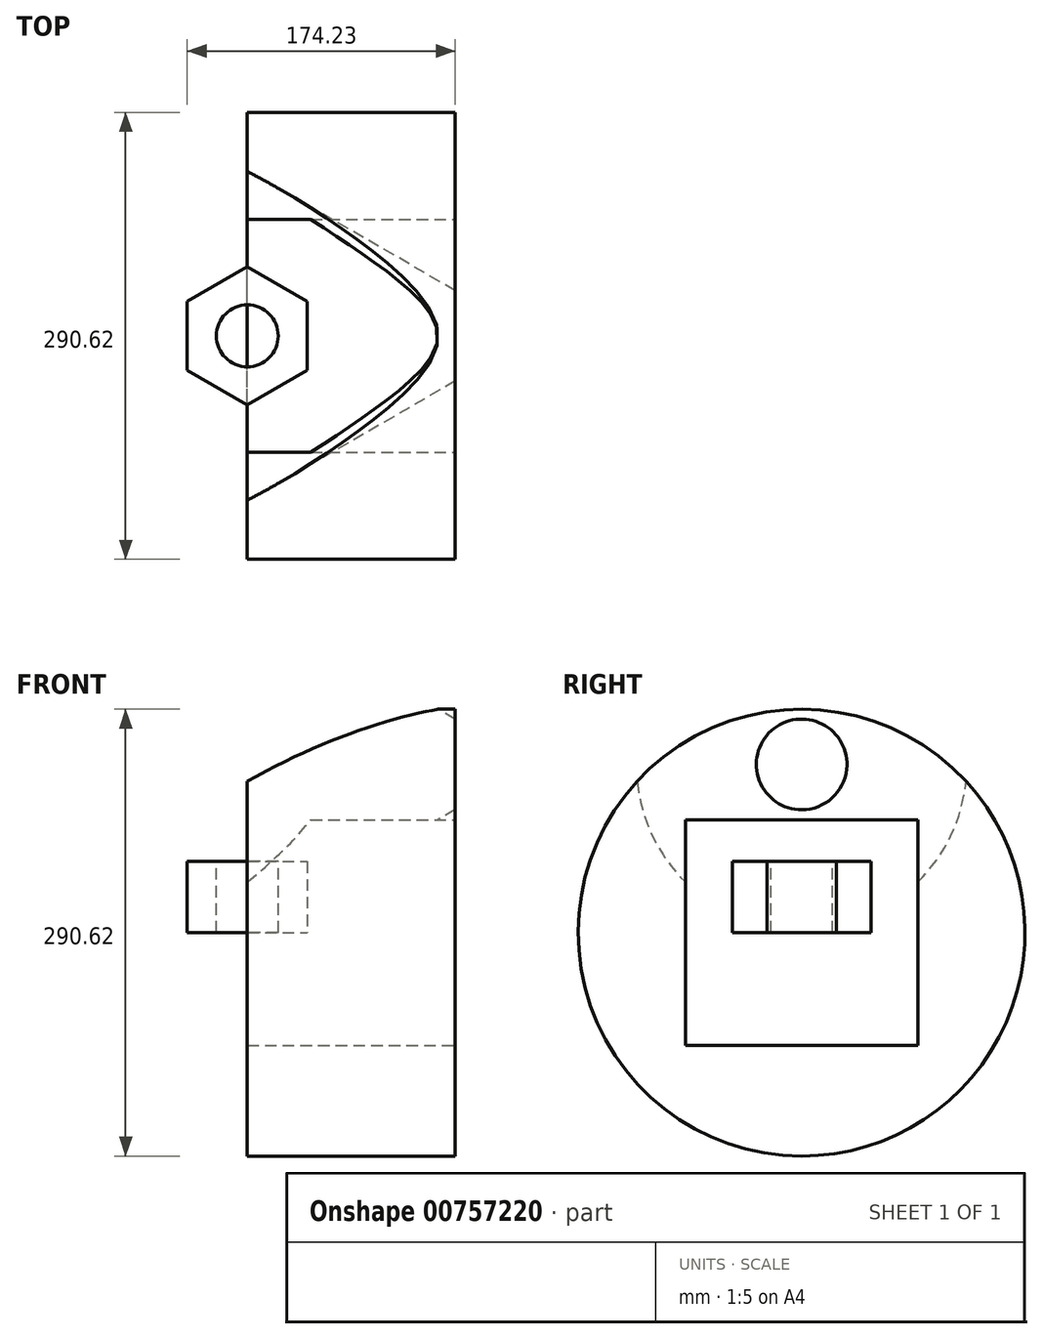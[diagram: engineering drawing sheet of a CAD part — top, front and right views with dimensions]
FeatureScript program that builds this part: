
annotation { "Feature Type Name" : "Feature", "Feature Type Description" : "" }
export const myFeature = defineFeature(function(context is Context, id is Id, definition is map)
    precondition{}
    {
        {
            var Q0;
            Q0=qCreatedBy(makeId("Top.planeOp"),FACE);
            var sketch = newSketch(context, id + "F0", { "sketchPlane" : qUnion([Q0])});
            skCircle(sketch, "E0.cCircle", {"center": v(0, 0) * mm, "radius": 44.06 * mm, "construction": true});
            skLineSegment(sketch, "E0.0", {"start": v(26.59, 38.63) * mm, "end": v(45.2, 12.5) * mm});
            skLineSegment(sketch, "E0.1", {"start": v(45.2, 12.5) * mm, "end": v(42.66, -19.48) * mm});
            skLineSegment(sketch, "E0.2", {"start": v(42.66, -19.48) * mm, "end": v(20.16, -42.34) * mm});
            skLineSegment(sketch, "E0.3", {"start": v(20.16, -42.34) * mm, "end": v(-11.77, -45.4) * mm});
            skLineSegment(sketch, "E0.4", {"start": v(-11.77, -45.4) * mm, "end": v(-38.2, -27.2) * mm});
            skLineSegment(sketch, "E0.5", {"start": v(-38.2, -27.2) * mm, "end": v(-46.75, 3.71) * mm});
            skLineSegment(sketch, "E0.6", {"start": v(-46.75, 3.71) * mm, "end": v(-33.42, 32.9) * mm});
            skLineSegment(sketch, "E0.7", {"start": v(-33.42, 32.9) * mm, "end": v(-4.46, 46.68) * mm});
            skLineSegment(sketch, "E0.8", {"start": v(-4.46, 46.68) * mm, "end": v(26.59, 38.63) * mm});
            skPoint(sketch, "E0.0.midPoint", {"position": v(35.9, 25.56) * mm});
            skSolve(sketch);
        }
        {
            var Q0;
            Q0=makeQuery(id+"F0.imprint","IMPRINT",FACE,{"disambiguationData":[TD([[makeQuery(id+"F0.imprint","IMPRINT",EDGE,{"derivedFrom":sQuery(id+"F0.wireOp",EDGE,"E0.0")}),-1.0]])]});
            extrude(context, id + "F1", {"entities" : qUnion([Q0]), "depth" : 67.3 * mm, "offsetDistance" : 25.4 * mm});
        }
        {
            var Q0;
            Q0=makeQuery(id+"F1.opExtrude","CAP_FACE",FACE,{"disambiguationData":[OSD([sQuery(id+"F0.wireOp",EDGE,"E0.0"),sQuery(id+"F0.wireOp",EDGE,"E0.1"),sQuery(id+"F0.wireOp",EDGE,"E0.2"),sQuery(id+"F0.wireOp",EDGE,"E0.3"),sQuery(id+"F0.wireOp",EDGE,"E0.4"),sQuery(id+"F0.wireOp",EDGE,"E0.5"),sQuery(id+"F0.wireOp",EDGE,"E0.6"),sQuery(id+"F0.wireOp",EDGE,"E0.7"),sQuery(id+"F0.wireOp",EDGE,"E0.8")])],"isStart":false});
            var sketch = newSketch(context, id + "F2", { "sketchPlane" : qUnion([Q0])});
            skCircle(sketch, "E1.cCircle", {"center": v(0, 0) * mm, "radius": 13.36 * mm, "construction": true});
            skLineSegment(sketch, "E1.0", {"start": v(13.36, 6.43) * mm, "end": v(13.36, -6.43) * mm});
            skLineSegment(sketch, "E1.1", {"start": v(13.36, -6.43) * mm, "end": v(3.3, -14.46) * mm});
            skLineSegment(sketch, "E1.2", {"start": v(3.3, -14.46) * mm, "end": v(-9.25, -11.6) * mm});
            skLineSegment(sketch, "E1.3", {"start": v(-9.25, -11.6) * mm, "end": v(-14.83, 0) * mm});
            skLineSegment(sketch, "E1.4", {"start": v(-14.83, 0) * mm, "end": v(-9.25, 11.6) * mm});
            skLineSegment(sketch, "E1.5", {"start": v(-9.25, 11.6) * mm, "end": v(3.3, 14.46) * mm});
            skLineSegment(sketch, "E1.6", {"start": v(3.3, 14.46) * mm, "end": v(13.36, 6.43) * mm});
            skPoint(sketch, "E1.0.midPoint", {"position": v(13.36, 0) * mm});
            skSolve(sketch);
        }
        {
            var Q0;
            Q0=makeQuery(id+"F2.imprint","IMPRINT",FACE,{"disambiguationData":[TD([[makeQuery(id+"F2.imprint","IMPRINT",EDGE,{"derivedFrom":sQuery(id+"F2.wireOp",EDGE,"E1.0")}),-1.0]])]});
            extrude(context, id + "F3", {"entities" : qUnion([Q0]), "operationType" : NewBodyOperationType.REMOVE, "oppositeDirection" : true, "depth" : 91.19 * mm, "offsetDistance" : 25.4 * mm});
        }
        {
            var Q0;
            Q0=qCreatedBy(makeId("Right.planeOp"),FACE);
            var sketch = newSketch(context, id + "F4", { "sketchPlane" : qUnion([Q0])});
            skCircle(sketch, "E2", {"center": v(0, 0) * mm, "radius": 145.31 * mm});
            skSolve(sketch);
        }
        {
            var Q0;
            Q0=makeQuery(id+"F4.imprint","IMPRINT",FACE,{"disambiguationData":[TD([[makeQuery(id+"F4.imprint","IMPRINT",EDGE,{"derivedFrom":sQuery(id+"F4.wireOp",EDGE,"E2")}),1.0]])]});
            extrude(context, id + "F5", {"entities" : qUnion([Q0]), "operationType" : NewBodyOperationType.ADD, "depth" : 135.2 * mm, "offsetDistance" : 25.4 * mm});
        }
        {
            var Q0;
            Q0=makeQuery(id+"F5.opExtrude","CAP_FACE",FACE,{"disambiguationData":[OSD([sQuery(id+"F4.wireOp",EDGE,"E2")])],"isStart":false});
            var sketch = newSketch(context, id + "F6", { "sketchPlane" : qUnion([Q0])});
            skLineSegment(sketch, "E3.bottom", {"start": v(-75.64, 73.41) * mm, "end": v(75.64, 73.41) * mm});
            skLineSegment(sketch, "E3.top", {"start": v(-75.64, -73.41) * mm, "end": v(75.64, -73.41) * mm});
            skLineSegment(sketch, "E3.left", {"start": v(-75.64, 73.41) * mm, "end": v(-75.64, -73.41) * mm});
            skLineSegment(sketch, "E3.right", {"start": v(75.64, 73.41) * mm, "end": v(75.64, -73.41) * mm});
            skPoint(sketch, "E3.middle", {"position": v(0, 0) * mm});
            skSolve(sketch);
        }
        {
            var Q0;
            Q0=makeQuery(id+"F6.imprint","IMPRINT",FACE,{"disambiguationData":[TD([[makeQuery(id+"F6.imprint","IMPRINT",EDGE,{"derivedFrom":sQuery(id+"F6.wireOp",EDGE,"E3.bottom")}),-1.0]])]});
            extrude(context, id + "F7", {"entities" : qUnion([Q0]), "operationType" : NewBodyOperationType.REMOVE, "oppositeDirection" : true, "depth" : 219.4 * mm, "offsetDistance" : 25.4 * mm});
        }
        {
            var Q0;
            Q0=makeQuery(id+"F5.opExtrude","CAP_FACE",FACE,{"disambiguationData":[OSD([sQuery(id+"F4.wireOp",EDGE,"E2")])],"isStart":false});
            var sketch = newSketch(context, id + "F8", { "sketchPlane" : qUnion([Q0])});
            skCircle(sketch, "E4", {"center": v(0, 109.4) * mm, "radius": 29.48 * mm});
            skSolve(sketch);
        }
        {
            var Q0;
            Q0 = qSketchRegion(id + "F8", true);
            var Q1;
            Q1=sQuery(id+"F8.wireOp",EDGE,"E4");
            extrude(context, id + "F9", {"entities" : qUnion([Q0]), "operationType" : NewBodyOperationType.REMOVE, "surfaceEntities" : qUnion([Q1]), "endBound" : BoundingType.THROUGH_ALL, "oppositeDirection" : true, "depth" : 25.4 * mm, "offsetDistance" : 25.4 * mm, "hasDraft" : true, "draftAngle" : 30 * degree});
        }
        {
            var Q0;
            Q0=qCreatedBy(makeId("Top.planeOp"),FACE);
            var sketch = newSketch(context, id + "F10", { "sketchPlane" : qUnion([Q0])});
            skCircle(sketch, "E5.cCircle", {"center": v(0, 0) * mm, "radius": 39.03 * mm, "construction": true});
            skLineSegment(sketch, "E5.0", {"start": v(39.03, 22.53) * mm, "end": v(39.03, -22.53) * mm});
            skLineSegment(sketch, "E5.1", {"start": v(39.03, -22.53) * mm, "end": v(0, -45.07) * mm});
            skLineSegment(sketch, "E5.2", {"start": v(0, -45.07) * mm, "end": v(-39.03, -22.53) * mm});
            skLineSegment(sketch, "E5.3", {"start": v(-39.03, -22.53) * mm, "end": v(-39.03, 22.53) * mm});
            skLineSegment(sketch, "E5.4", {"start": v(-39.03, 22.53) * mm, "end": v(0, 45.07) * mm});
            skLineSegment(sketch, "E5.5", {"start": v(0, 45.07) * mm, "end": v(39.03, 22.53) * mm});
            skPoint(sketch, "E5.0.midPoint", {"position": v(39.03, 0) * mm});
            skSolve(sketch);
        }
        {
            var Q0;
            Q0=makeQuery(id+"F10.imprint","IMPRINT",FACE,{"disambiguationData":[TD([[makeQuery(id+"F10.imprint","IMPRINT",EDGE,{"derivedFrom":sQuery(id+"F10.wireOp",EDGE,"E5.0")}),-1.0]])]});
            extrude(context, id + "F11", {"entities" : qUnion([Q0]), "depth" : 46.23 * mm, "offsetDistance" : 25.4 * mm});
        }
        {
            var Q0;
            Q0=makeQuery(id+"F11.opExtrude","CAP_FACE",FACE,{"disambiguationData":[OSD([sQuery(id+"F10.wireOp",EDGE,"E5.0"),sQuery(id+"F10.wireOp",EDGE,"E5.1"),sQuery(id+"F10.wireOp",EDGE,"E5.2"),sQuery(id+"F10.wireOp",EDGE,"E5.3"),sQuery(id+"F10.wireOp",EDGE,"E5.4"),sQuery(id+"F10.wireOp",EDGE,"E5.5")])],"isStart":false});
            var sketch = newSketch(context, id + "F12", { "sketchPlane" : qUnion([Q0])});
            skCircle(sketch, "E6", {"center": v(0, 0) * mm, "radius": 20.1 * mm});
            skSolve(sketch);
        }
        {
            var Q0;
            Q0=makeQuery(id+"F12.imprint","IMPRINT",FACE,{"disambiguationData":[TD([[makeQuery(id+"F12.imprint","IMPRINT",EDGE,{"derivedFrom":sQuery(id+"F12.wireOp",EDGE,"E6")}),1.0]])]});
            extrude(context, id + "F13", {"entities" : qUnion([Q0]), "operationType" : NewBodyOperationType.REMOVE, "oppositeDirection" : true, "depth" : 60.96 * mm, "offsetDistance" : 25.4 * mm});
        }
    });
